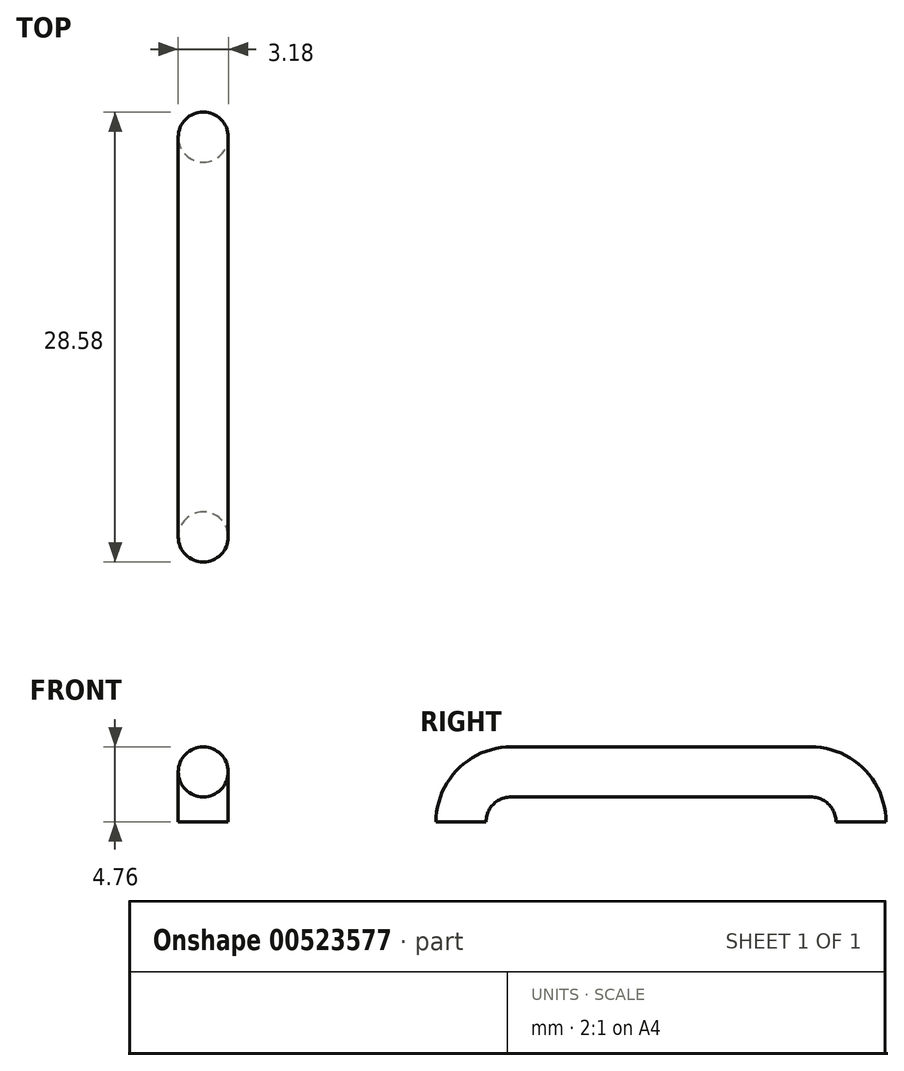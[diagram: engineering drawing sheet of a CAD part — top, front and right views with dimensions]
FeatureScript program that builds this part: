
annotation { "Feature Type Name" : "Feature", "Feature Type Description" : "" }
export const myFeature = defineFeature(function(context is Context, id is Id, definition is map)
    precondition{}
    {
        {
            var Q0;
            Q0=qCreatedBy(makeId("Right.planeOp"),FACE);
            var sketch = newSketch(context, id + "F0", { "sketchPlane" : qUnion([Q0])});
            skLineSegment(sketch, "E0", {"start": v(0, 0) * mm, "end": v(0, 0) * mm});
            skLineSegment(sketch, "E1", {"start": v(3.18, 3.18) * mm, "end": v(22.23, 3.18) * mm});
            skLineSegment(sketch, "E2", {"start": v(25.4, 0) * mm, "end": v(25.4, 0) * mm});
            skPoint(sketch, "E3.visualSharp", {"position": v(0, 3.18) * mm});
            skArc(sketch, "E3.filletArc", {"start": v(3.18, 3.18) * mm, "mid": v(0.93, 2.25) * mm, "end": v(0, 0) * mm});
            skPoint(sketch, "E4.visualSharp", {"position": v(25.4, 3.18) * mm});
            skArc(sketch, "E4.filletArc", {"start": v(25.4, 0) * mm, "mid": v(24.47, 2.25) * mm, "end": v(22.23, 3.17) * mm});
            skSolve(sketch);
        }
        {
            var Q0;
            Q0=qCreatedBy(makeId("Top.planeOp"),FACE);
            var sketch = newSketch(context, id + "F1", { "sketchPlane" : qUnion([Q0])});
            skCircle(sketch, "E5", {"center": v(0, 0) * mm, "radius": 1.59 * mm});
            skSolve(sketch);
        }
        {
            var Q0;
            Q0=makeQuery(id+"F1.imprint","IMPRINT",FACE,{"disambiguationData":[TD([[makeQuery(id+"F1.imprint","IMPRINT",EDGE,{"derivedFrom":sQuery(id+"F1.wireOp",EDGE,"E5")}),1.0]])]});
            var Q1;
            Q1=sQuery(id+"F0.wireOp",EDGE,"E3.filletArc");
            var Q2;
            Q2=sQuery(id+"F0.wireOp",EDGE,"E1");
            var Q3;
            Q3=sQuery(id+"F0.wireOp",EDGE,"E4.filletArc");
            sweep(context, id + "F2", {"profiles" : qUnion([Q0]), "path" : qUnion([Q1, Q2, Q3])});
        }
    });
